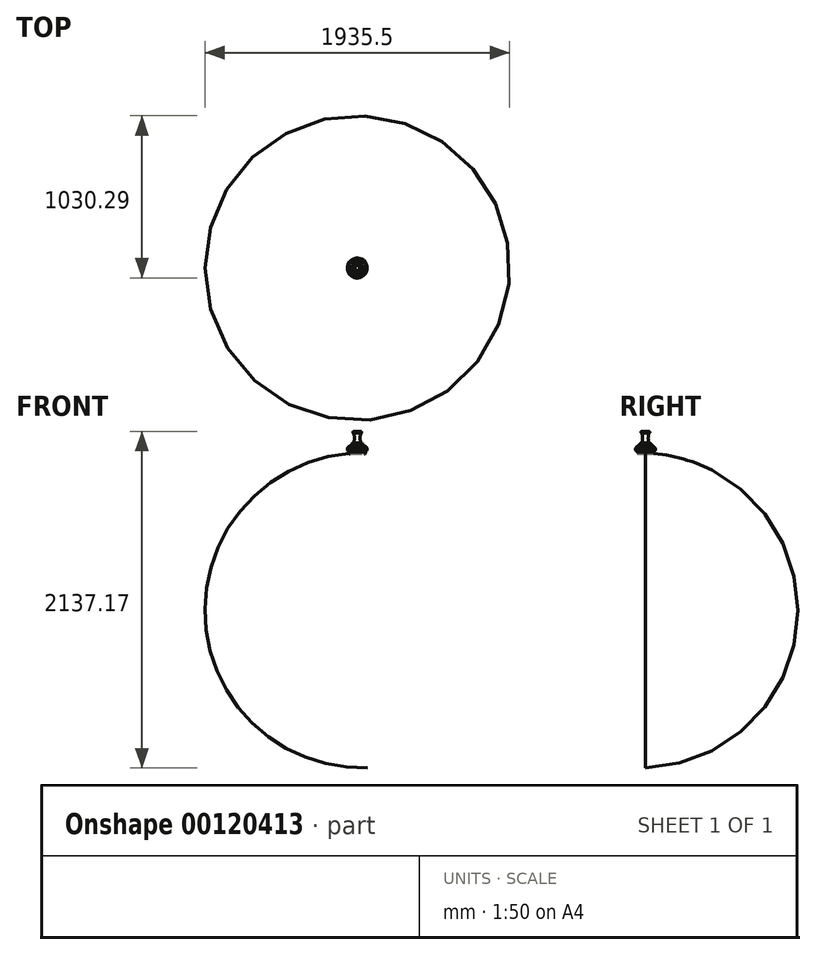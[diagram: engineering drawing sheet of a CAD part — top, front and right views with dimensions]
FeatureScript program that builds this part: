
annotation { "Feature Type Name" : "Feature", "Feature Type Description" : "" }
export const myFeature = defineFeature(function(context is Context, id is Id, definition is map)
    precondition{}
    {
        {
            var Q0;
            Q0=qCreatedBy(makeId("Front.planeOp"),FACE);
            var sketch = newSketch(context, id + "F0", { "sketchPlane" : qUnion([Q0])});
            skArc(sketch, "E0", {"start": v(0, -65.16) * mm, "mid": v(-19.04, -64.73) * mm, "end": v(-38.08, -64.66) * mm});
            skArc(sketch, "E1", {"start": v(-49.1, -57.4) * mm, "mid": v(-49.66, -70.24) * mm, "end": v(-38.08, -64.66) * mm});
            skArc(sketch, "E2", {"start": v(-62.39, -40.1) * mm, "mid": v(-59.38, -51.54) * mm, "end": v(-49.1, -57.4) * mm});
            skArc(sketch, "E3", {"start": v(-53.62, -23.32) * mm, "mid": v(-59.93, -30.7) * mm, "end": v(-62.39, -40.1) * mm});
            skArc(sketch, "E4", {"start": v(-37.08, -17.56) * mm, "mid": v(-45.65, -19.58) * mm, "end": v(-53.62, -23.32) * mm});
            skArc(sketch, "E5", {"start": v(-24.8, -3.03) * mm, "mid": v(-17.58, 29.8) * mm, "end": v(-24.8, 62.61) * mm});
            skPoint(sketch, "E6.endSnap0", {"position": v(-59.38, -51.54) * mm});
            skLineSegment(sketch, "E7", {"start": v(-38.08, -60.9) * mm, "end": v(0, -60.9) * mm});
            skLineSegment(sketch, "E8", {"start": v(0, -60.9) * mm, "end": v(0, -65.16) * mm});
            skArc(sketch, "E9", {"start": v(-24.8, -3.03) * mm, "mid": v(-35.48, -6.46) * mm, "end": v(-37.08, -17.56) * mm});
            skLineSegment(sketch, "E10", {"start": v(-24.8, 72.64) * mm, "end": v(-22.35, 72.26) * mm});
            skArc(sketch, "E11", {"start": v(-22.35, 72.26) * mm, "mid": v(-23.62, 67.44) * mm, "end": v(-22.35, 62.61) * mm});
            skArc(sketch, "E12", {"start": v(-22.35, -5.1) * mm, "mid": v(-15.74, 28.76) * mm, "end": v(-22.35, 62.61) * mm});
            skArc(sketch, "E13", {"start": v(-22.35, -5.1) * mm, "mid": v(-32.64, -7.15) * mm, "end": v(-34.02, -17.56) * mm});
            skArc(sketch, "E14", {"start": v(-53.17, -25.28) * mm, "mid": v(-42.27, -24.7) * mm, "end": v(-34.02, -17.56) * mm});
            skArc(sketch, "E15", {"start": v(-53.17, -25.28) * mm, "mid": v(-60.32, -37.59) * mm, "end": v(-57.54, -51.54) * mm});
            skArc(sketch, "E16", {"start": v(-38.08, -60.9) * mm, "mid": v(-47.71, -56.03) * mm, "end": v(-57.54, -51.54) * mm});
            skArc(sketch, "E17", {"start": v(-24.8, 72.64) * mm, "mid": v(-27.6, 67.62) * mm, "end": v(-24.8, 62.61) * mm});
            skSolve(sketch);
        }
        {
            var Q0;
            Q0=makeQuery(id+"F0.imprint","IMPRINT",FACE,{"disambiguationData":[TD([[makeQuery(id+"F0.imprint","IMPRINT",EDGE,{"derivedFrom":sQuery(id+"F0.wireOp",EDGE,"E0")}),-1.0]])]});
            var Q1;
            Q1=sQuery(id+"F0.wireOp",EDGE,"E8");
            revolve(context, id + "F1", {"entities" : qUnion([Q0]), "axis" : qUnion([Q1]), "revolveType" : RevolveType.FULL});
        }
    });
